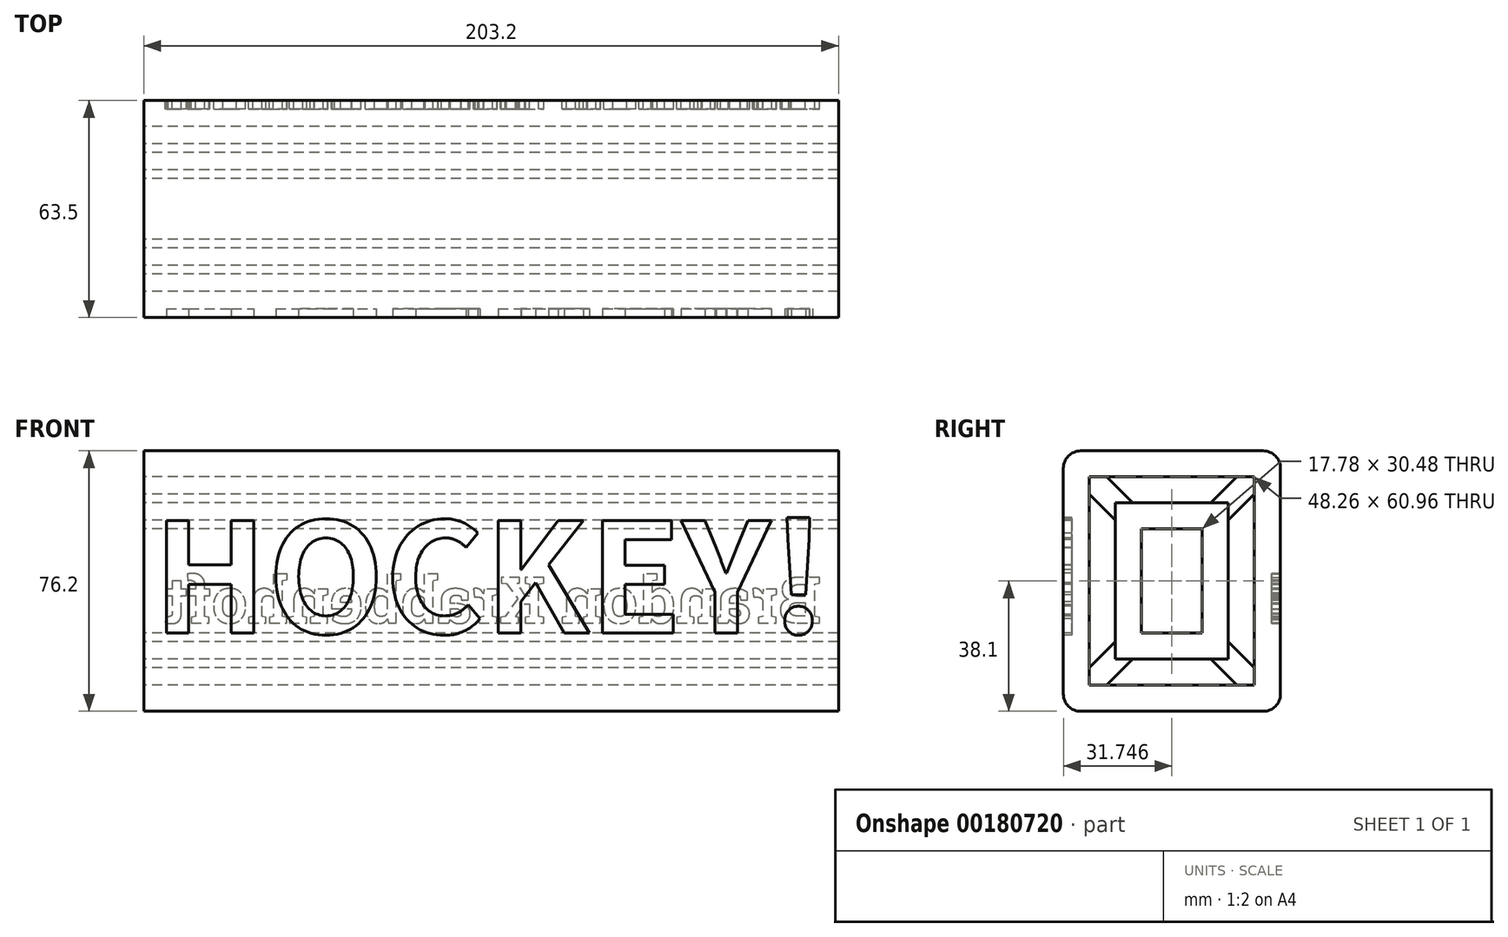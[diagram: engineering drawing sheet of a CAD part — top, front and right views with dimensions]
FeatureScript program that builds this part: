
annotation { "Feature Type Name" : "Feature", "Feature Type Description" : "" }
export const myFeature = defineFeature(function(context is Context, id is Id, definition is map)
    precondition{}
    {
        {
            var Q0;
            Q0=qCreatedBy(makeId("Right.planeOp"),FACE);
            var sketch = newSketch(context, id + "F0", { "sketchPlane" : qUnion([Q0])});
            skLineSegment(sketch, "E0.bottom", {"start": v(-29.21, 42.84) * mm, "end": v(34.29, 42.84) * mm});
            skLineSegment(sketch, "E0.top", {"start": v(-29.21, -33.36) * mm, "end": v(34.29, -33.36) * mm});
            skLineSegment(sketch, "E0.left", {"start": v(-29.21, 42.84) * mm, "end": v(-29.21, -33.36) * mm});
            skLineSegment(sketch, "E0.right", {"start": v(34.29, 42.84) * mm, "end": v(34.29, -33.36) * mm});
            skLineSegment(sketch, "E1.bottom", {"start": v(-21.6, 35.22) * mm, "end": v(26.67, 35.22) * mm});
            skLineSegment(sketch, "E1.top", {"start": v(-21.6, -25.74) * mm, "end": v(26.67, -25.74) * mm});
            skLineSegment(sketch, "E1.left", {"start": v(-21.6, 35.22) * mm, "end": v(-21.6, -25.74) * mm});
            skLineSegment(sketch, "E1.right", {"start": v(26.67, 35.22) * mm, "end": v(26.67, -25.74) * mm});
            skSolve(sketch);
        }
        {
            var Q0;
            Q0=makeQuery(id+"F0.imprint","IMPRINT",FACE,{"disambiguationData":[TD([[makeQuery(id+"F0.imprint","IMPRINT",EDGE,{"derivedFrom":sQuery(id+"F0.wireOp",EDGE,"E0.bottom")}),-1.0]])]});
            extrude(context, id + "F1", {"entities" : qUnion([Q0]), "depth" : 203.2 * mm});
        }
        {
            var Q0;
            Q0=makeQuery(id+"F1.opExtrude","CAP_FACE",FACE,{"disambiguationData":[OSD([sQuery(id+"F0.wireOp",EDGE,"E0.bottom"),sQuery(id+"F0.wireOp",EDGE,"E0.top"),sQuery(id+"F0.wireOp",EDGE,"E0.left"),sQuery(id+"F0.wireOp",EDGE,"E0.right"),sQuery(id+"F0.wireOp",EDGE,"E1.bottom"),sQuery(id+"F0.wireOp",EDGE,"E1.top"),sQuery(id+"F0.wireOp",EDGE,"E1.left"),sQuery(id+"F0.wireOp",EDGE,"E1.right")])],"isStart":true});
            var sketch = newSketch(context, id + "F2", { "sketchPlane" : qUnion([Q0])});
            skLineSegment(sketch, "E2.bottom", {"start": v(-19.05, 27.6) * mm, "end": v(13.97, 27.6) * mm});
            skLineSegment(sketch, "E2.top", {"start": v(-19.05, -18.12) * mm, "end": v(13.97, -18.12) * mm});
            skLineSegment(sketch, "E2.left", {"start": v(-19.05, 27.6) * mm, "end": v(-19.05, -18.12) * mm});
            skLineSegment(sketch, "E2.right", {"start": v(13.97, 27.6) * mm, "end": v(13.97, -18.12) * mm});
            skLineSegment(sketch, "E3.bottom", {"start": v(-11.43, 19.98) * mm, "end": v(6.35, 19.98) * mm});
            skLineSegment(sketch, "E3.top", {"start": v(-11.43, -10.5) * mm, "end": v(6.35, -10.5) * mm});
            skLineSegment(sketch, "E3.left", {"start": v(-11.43, 19.98) * mm, "end": v(-11.43, -10.5) * mm});
            skLineSegment(sketch, "E3.right", {"start": v(6.35, 19.98) * mm, "end": v(6.35, -10.5) * mm});
            skSolve(sketch);
        }
        {
            var Q0;
            Q0=makeQuery(id+"F2.imprint","IMPRINT",FACE,{"disambiguationData":[TD([[makeQuery(id+"F2.imprint","IMPRINT",EDGE,{"derivedFrom":sQuery(id+"F2.wireOp",EDGE,"E2.bottom")}),-1.0]])]});
            extrude(context, id + "F3", {"entities" : qUnion([Q0]), "oppositeDirection" : true, "depth" : 203.2 * mm});
        }
        {
            var Q0;
            Q0=makeQuery(id+"F1.opExtrude","CAP_FACE",FACE,{"disambiguationData":[OSD([sQuery(id+"F0.wireOp",EDGE,"E0.bottom"),sQuery(id+"F0.wireOp",EDGE,"E0.top"),sQuery(id+"F0.wireOp",EDGE,"E0.left"),sQuery(id+"F0.wireOp",EDGE,"E0.right"),sQuery(id+"F0.wireOp",EDGE,"E1.bottom"),sQuery(id+"F0.wireOp",EDGE,"E1.top"),sQuery(id+"F0.wireOp",EDGE,"E1.left"),sQuery(id+"F0.wireOp",EDGE,"E1.right")])],"isStart":true});
            var sketch = newSketch(context, id + "F4", { "sketchPlane" : qUnion([Q0])});
            skLineSegment(sketch, "E4", {"start": v(-21.59, 35.22) * mm, "end": v(-13.97, 27.6) * mm});
            skLineSegment(sketch, "E5", {"start": v(-26.67, 30.14) * mm, "end": v(-19.05, 22.52) * mm});
            skLineSegment(sketch, "E6", {"start": v(16.51, 35.22) * mm, "end": v(8.9, 27.6) * mm});
            skLineSegment(sketch, "E7", {"start": v(21.6, 30.14) * mm, "end": v(13.97, 22.52) * mm});
            skLineSegment(sketch, "E8", {"start": v(-19.05, -13.04) * mm, "end": v(-26.67, -20.66) * mm});
            skLineSegment(sketch, "E9", {"start": v(-13.97, -18.12) * mm, "end": v(-21.59, -25.74) * mm});
            skLineSegment(sketch, "E10", {"start": v(8.9, -18.12) * mm, "end": v(16.51, -25.74) * mm});
            skLineSegment(sketch, "E11", {"start": v(13.97, -13.04) * mm, "end": v(21.6, -20.66) * mm});
            skLineSegment(sketch, "E12", {"start": v(-13.97, -18.12) * mm, "end": v(-19.05, -18.12) * mm});
            skLineSegment(sketch, "E13", {"start": v(-19.05, -18.12) * mm, "end": v(-19.05, -13.04) * mm});
            skLineSegment(sketch, "E14", {"start": v(-19.05, 22.52) * mm, "end": v(-19.05, 27.6) * mm});
            skLineSegment(sketch, "E15", {"start": v(-19.05, 27.6) * mm, "end": v(-13.97, 27.6) * mm});
            skLineSegment(sketch, "E16", {"start": v(8.9, 27.6) * mm, "end": v(13.97, 27.6) * mm});
            skLineSegment(sketch, "E17", {"start": v(13.97, 27.6) * mm, "end": v(13.97, 22.52) * mm});
            skLineSegment(sketch, "E18", {"start": v(13.97, -13.04) * mm, "end": v(13.97, -18.12) * mm});
            skLineSegment(sketch, "E19", {"start": v(13.97, -18.12) * mm, "end": v(8.9, -18.12) * mm});
            skSolve(sketch);
        }
        {
            var Q0;
            {var subQ1=sQuery(id+"F4.wireOp",EDGE,"E4");Q0=makeQuery(id+"F4.imprint","IMPRINT",FACE,{"disambiguationData":[TD([[makeQuery(id+"F4.imprint","IMPRINT",EDGE,{"derivedFrom":subQ1}),-1.0]])]});}
            var Q1;
            {var subQ1=sQuery(id+"F4.wireOp",EDGE,"E6");Q1=makeQuery(id+"F4.imprint","IMPRINT",FACE,{"disambiguationData":[TD([[makeQuery(id+"F4.imprint","IMPRINT",EDGE,{"derivedFrom":subQ1}),1.0]])]});}
            var Q2;
            {var subQ1=sQuery(id+"F4.wireOp",EDGE,"E10");Q2=makeQuery(id+"F4.imprint","IMPRINT",FACE,{"disambiguationData":[TD([[makeQuery(id+"F4.imprint","IMPRINT",EDGE,{"derivedFrom":subQ1}),1.0]])]});}
            var Q3;
            {var subQ1=sQuery(id+"F4.wireOp",EDGE,"E8");Q3=makeQuery(id+"F4.imprint","IMPRINT",FACE,{"disambiguationData":[TD([[makeQuery(id+"F4.imprint","IMPRINT",EDGE,{"derivedFrom":subQ1}),1.0]])]});}
            extrude(context, id + "F5", {"entities" : qUnion([Q0, Q1, Q2, Q3]), "oppositeDirection" : true, "depth" : 203.2 * mm});
        }
        {
            var Q0;
            Q0=makeQuery(id+"F1.opExtrude","SWEPT_EDGE",EDGE,{"disambiguationData":[OSD([sQuery(id+"F0.wireOp",EDGE,"E0.bottom"),sQuery(id+"F0.wireOp",EDGE,"E0.left")])]});
            var Q1;
            Q1=makeQuery(id+"F1.opExtrude","SWEPT_EDGE",EDGE,{"disambiguationData":[OSD([sQuery(id+"F0.wireOp",EDGE,"E0.bottom"),sQuery(id+"F0.wireOp",EDGE,"E0.right")])]});
            var Q2;
            Q2=makeQuery(id+"F1.opExtrude","SWEPT_EDGE",EDGE,{"disambiguationData":[OSD([sQuery(id+"F0.wireOp",EDGE,"E0.top"),sQuery(id+"F0.wireOp",EDGE,"E0.right")])]});
            var Q3;
            Q3=makeQuery(id+"F1.opExtrude","SWEPT_EDGE",EDGE,{"disambiguationData":[OSD([sQuery(id+"F0.wireOp",EDGE,"E0.top"),sQuery(id+"F0.wireOp",EDGE,"E0.left")])]});
            fillet(context, id + "F6", {"entities" : qUnion([Q0, Q1, Q2, Q3]), "radius" : 5.08 * mm, "tangentPropagation" : true, "allowEdgeOverflow" : false});
        }
        {
            var Q0;
            Q0=makeQuery(id+"F1.opExtrude","SWEPT_FACE",FACE,{"disambiguationData":[OSD([sQuery(id+"F0.wireOp",EDGE,"E0.right")])]});
            var sketch = newSketch(context, id + "F7", { "sketchPlane" : qUnion([Q0])});
            skText(sketch, "E20", { "text": "Brandon Krabbenhoft ", "fontName": "RobotoSlab-Bold.ttf"});
            const initialGuessF7  = {"E20": [-0.19812, -0.0075, 1, 0, 0.01351]};
            skSetInitialGuess(sketch, initialGuessF7);
            skSolve(sketch);
        }
        {
            var Q0;
            Q0 = qSketchRegion(id + "F7", true);
            extrude(context, id + "F8", {"entities" : qUnion([Q0]), "operationType" : NewBodyOperationType.REMOVE, "oppositeDirection" : true, "depth" : 2.54 * mm});
        }
        {
            var Q0;
            Q0=makeQuery(id+"F1.opExtrude","SWEPT_FACE",FACE,{"disambiguationData":[OSD([sQuery(id+"F0.wireOp",EDGE,"E0.left")])]});
            var sketch = newSketch(context, id + "F9", { "sketchPlane" : qUnion([Q0])});
            skText(sketch, "E21", { "text": "HOCKEY!", "fontName": "NotoSansCJKkr-Bold.otf"});
            const initialGuessF9  = {"E21": [0.00254, -0.0105, 1, 0, 0.032]};
            skSetInitialGuess(sketch, initialGuessF9);
            skSolve(sketch);
        }
        {
            var Q0;
            Q0 = qSketchRegion(id + "F9", true);
            extrude(context, id + "F10", {"entities" : qUnion([Q0]), "operationType" : NewBodyOperationType.REMOVE, "oppositeDirection" : true, "depth" : 2.54 * mm});
        }
    });
